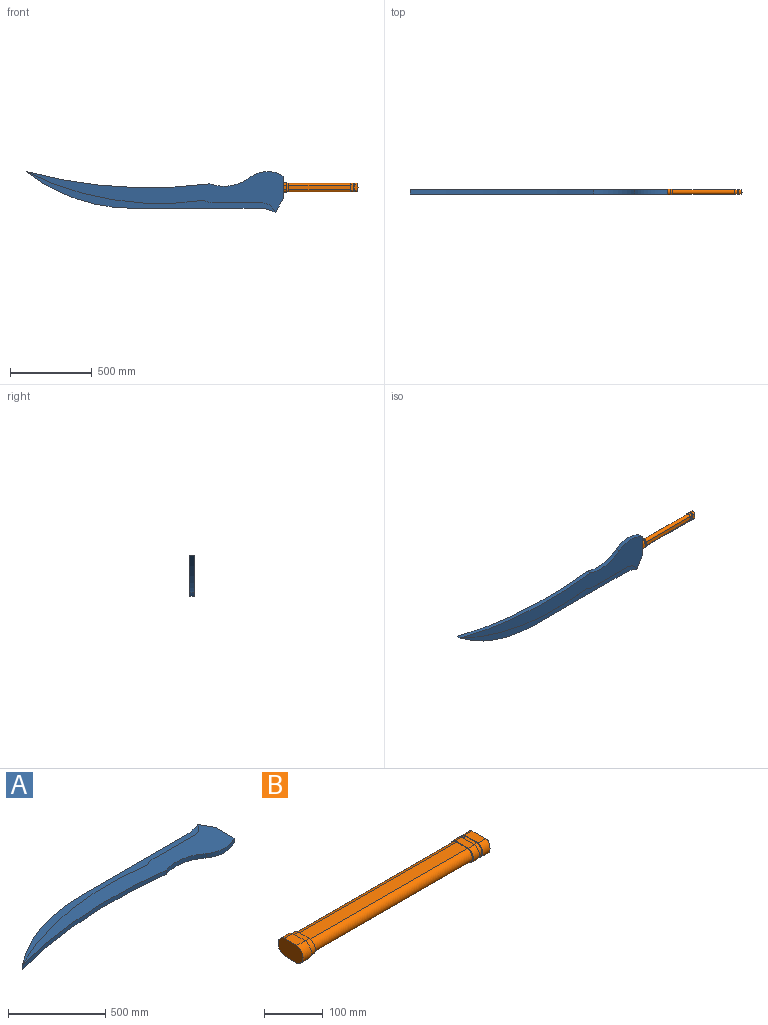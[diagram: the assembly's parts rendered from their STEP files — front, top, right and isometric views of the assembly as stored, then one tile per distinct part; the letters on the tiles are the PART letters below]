
ASSEMBLY  parts=2 mates=1
PART A: 20 faces, bbox 1575x250x27 mm
  f0: plane 1575x250mm, normal (0,0,1), area 149130.2mm2, adj f1,f2,f3,f4,f5,f9,f10,f11
  f1: plane 135x27mm, normal (1,0,0), area 3645mm2, adj f0,f2,f5,f14
  f2: cylinder r=175mm len=200mm, axis (0,0,1), area 5748.6mm2, adj f0,f1,f3,f14
  f3: cylinder r=263.37mm len=250mm, axis (0,0,1), area 7141.8mm2, adj f0,f2,f4,f14
  f4: cylinder r=2897.78mm len=1125mm, axis (0,0,1), area 30637.8mm2, adj f0,f3,f8,f11,f14,f17
  f5: plane 85x49mm, normal (0.87,0.5,0), area 2649mm2, adj f0,f1,f7,f10,f14,f16
  f6: plane 776x25mm, normal (0,1,0), area 19400mm2, adj f7,f8,f13,f19
  f7: cylinder r=212.5mm len=100mm, axis (0,0,1), area 2602.9mm2, adj f5,f6,f13,f19
  f8: cylinder r=1065.27mm len=650mm, axis (0,0,1), area 17509.7mm2, adj f4,f6,f13,f19
  f9: plane 300.21x1mm, normal (0,1,0), area 300.2mm2, adj f0,f10,f12,f13
  f10: cylinder r=86.63mm len=76.93mm, axis (0,0,1), area 102mm2, adj f0,f5,f9,f13
  f11: cylinder r=1819.87mm len=1090.47mm, axis (0,0,1), area 1122.2mm2, adj f0,f4,f12,f13
  f12: cylinder r=97.88mm len=58.4mm, axis (0,0,1), area 61.8mm2, adj f0,f9,f11,f13
  f13: plane 1526x250mm, normal (0,0,1), area 53433.9mm2, adj f6,f7,f8,f9,f10,f11,f12
  f14: plane 1575x250mm, normal (0,0,-1), area 149130.2mm2, adj f1,f2,f3,f4,f5,f15,f16,f17
  f15: plane 300.21x1mm, normal (0,1,0), area 300.2mm2, adj f14,f16,f18,f19
  f16: cylinder r=86.63mm len=76.93mm, axis (0,0,-1), area 102mm2, adj f5,f14,f15,f19
  f17: cylinder r=1819.87mm len=1090.47mm, axis (0,0,-1), area 1122.2mm2, adj f4,f14,f18,f19
  f18: cylinder r=97.88mm len=58.4mm, axis (0,0,-1), area 61.8mm2, adj f14,f15,f17,f19
  f19: plane 1526x250mm, normal (0,0,-1), area 53433.9mm2, adj f6,f7,f8,f15,f16,f17,f18
PART B: 34 faces, bbox 456x60x36.4 mm
  f0: plane 32.27x15mm, normal (0,0,1), area 484mm2, adj f1,f2,f32,f33
  f1: plane 54x30mm, normal (1,0,0), area 249.3mm2, adj f0,f3,f28,f29,f30,f31,f32,f33
  f2: plane 54x30mm, normal (-1,0,0), area 249.3mm2, adj f0,f3,f4,f5,f6,f7,f32,f33
  f3: plane 32.27x15mm, normal (0,0,-1), area 484mm2, adj f1,f2,f32,f33
  f4: plane 379x26mm, normal (0,0,1), area 9854mm2, adj f2,f6,f7,f10
  f5: plane 379x26mm, normal (0,0,-1), area 9854mm2, adj f2,f6,f7,f10
  f6: cylinder r=13.59mm len=379mm, axis (1,0,0), area 14974.7mm2, adj f2,f4,f5,f10
  f7: cylinder r=13.59mm len=379mm, axis (1,0,0), area 14974.7mm2, adj f2,f4,f5,f10
  f8: plane 60x36.38mm, normal (-1,0,0), area 1911.9mm2, adj f15,f16,f17,f18
  f9: plane 60x36.38mm, normal (1,0,0), area 370mm2, adj f11,f12,f13,f14,f15,f16,f17,f18
  f10: plane 54.97x32mm, normal (1,0,0), area 345.8mm2, adj f4,f5,f6,f7,f11,f12,f13,f14
  f11: cylinder r=16.08mm len=32mm, axis (1,0,0), area 567.9mm2, adj f9,f10,f12,f14
  f12: plane 26x12mm, normal (0,0,-1), area 312mm2, adj f9,f10,f11,f13
  f13: cylinder r=16.08mm len=32mm, axis (1,0,0), area 567.9mm2, adj f9,f10,f12,f14
  f14: plane 26x12mm, normal (0,0,1), area 312mm2, adj f9,f10,f11,f13
  f15: cylinder r=18.59mm len=36.38mm, axis (1,0,0), area 1012.9mm2, adj f8,f9,f16,f18
  f16: plane 30.52x20mm, normal (0,0,-1), area 610.5mm2, adj f8,f9,f15,f17
  f17: cylinder r=18.59mm len=36.38mm, axis (1,0,0), area 1012.9mm2, adj f8,f9,f16,f18
  f18: plane 30.52x20mm, normal (0,0,1), area 610.5mm2, adj f8,f9,f15,f17
  f19: cylinder r=82.15mm len=27.13mm, axis (0,0,1), area 364.5mm2, adj f20,f22,f24
  f20: cylinder r=26.71mm len=43.04mm, axis (0,-1,0), area 403.3mm2, adj f19,f21,f24,f25,f26
  f21: cylinder r=82.15mm len=27.13mm, axis (0,0,1), area 364.4mm2, adj f20,f22,f26
  f22: cylinder r=26.71mm len=43.04mm, axis (0,-1,0), area 403.3mm2, adj f19,f21,f23,f24,f26
  f23: plane 32.27x17.39mm, normal (0,0,-1), area 561.1mm2, adj f22,f24,f26,f27
  f24: cylinder r=15.73mm len=30mm, axis (1,0,0), area 719.4mm2, adj f19,f20,f22,f23,f25,f27
  f25: plane 32.27x17.39mm, normal (0,0,1), area 561.1mm2, adj f20,f24,f26,f27
  f26: cylinder r=15.73mm len=30mm, axis (1,0,0), area 719.4mm2, adj f20,f21,f22,f23,f25,f27
  f27: plane 54.27x30mm, normal (-1,0,0), area 256.2mm2, adj f23,f24,f25,f26,f28,f29,f30,f31
  f28: cylinder r=13.59mm len=27mm, axis (1,0,0), area 316.1mm2, adj f1,f27,f30,f31
  f29: cylinder r=13.59mm len=27mm, axis (1,0,0), area 316.1mm2, adj f1,f27,f30,f31
  f30: plane 26x8mm, normal (0,0,-1), area 208mm2, adj f1,f27,f28,f29
  f31: plane 26x8mm, normal (0,0,1), area 208mm2, adj f1,f27,f28,f29
  f32: cylinder r=15.79mm len=30mm, axis (1,0,0), area 593.8mm2, adj f0,f1,f2,f3
  f33: cylinder r=15.79mm len=30mm, axis (1,0,0), area 593.8mm2, adj f0,f1,f2,f3
PLACE A rot(axis=(-1,0,0),90deg) t=(-1434.16,13.5,179.14)mm
PLACE B rot(axis=(-1,0,0),90deg) t=(222.33,13.5,77.5)mm
MATE fastened B.f8 <-> A.f1  axis (-1,0,0) through (97.98,13.5,77.5)mm
